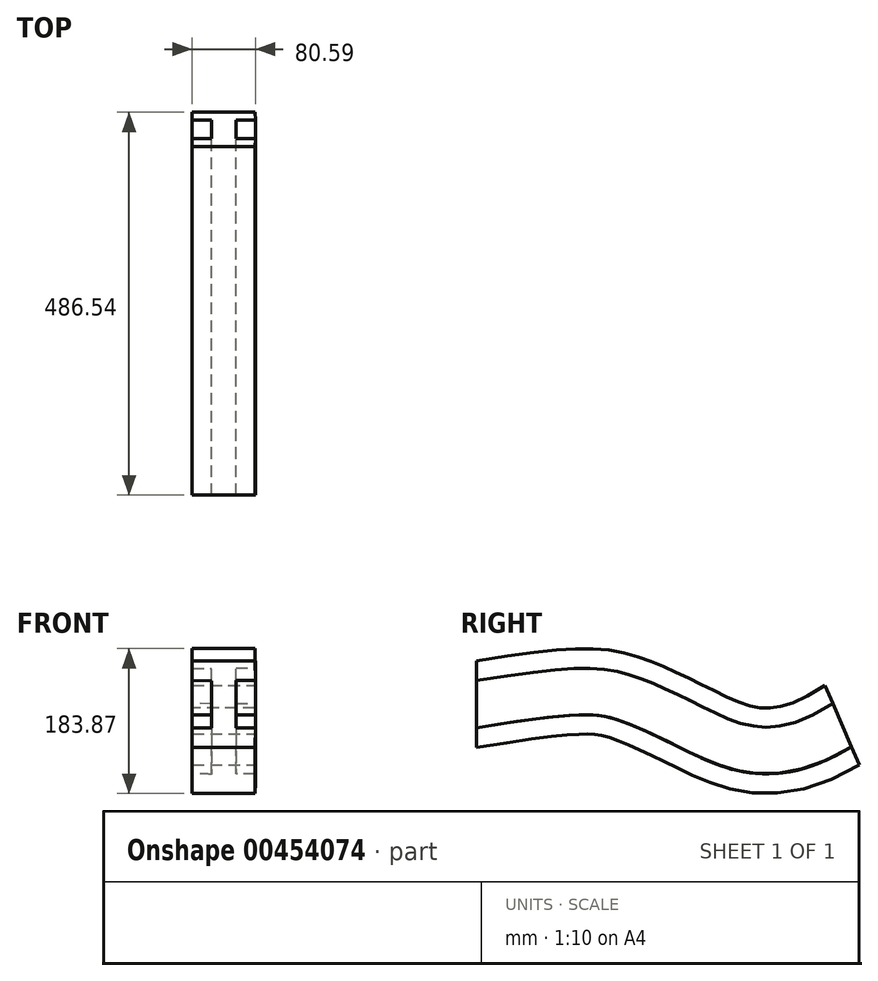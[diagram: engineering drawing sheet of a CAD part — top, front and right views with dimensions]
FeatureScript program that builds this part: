
annotation { "Feature Type Name" : "Feature", "Feature Type Description" : "" }
export const myFeature = defineFeature(function(context is Context, id is Id, definition is map)
    precondition{}
    {
        {
            var Q0;
            Q0=qCreatedBy(makeId("Front.planeOp"),FACE);
            var sketch = newSketch(context, id + "F0", { "sketchPlane" : qUnion([Q0])});
            skLineSegment(sketch, "E0", {"start": v(-41.1, 54.65) * mm, "end": v(38.9, 54.65) * mm});
            skLineSegment(sketch, "E1", {"start": v(-40.8, -55.35) * mm, "end": v(39.2, -55.35) * mm});
            skLineSegment(sketch, "E2", {"start": v(-16.1, 29.23) * mm, "end": v(-16.1, -30.77) * mm});
            skLineSegment(sketch, "E3", {"start": v(14.5, 29.66) * mm, "end": v(14.5, -30.34) * mm});
            skLineSegment(sketch, "E4", {"start": v(-41.1, 54.65) * mm, "end": v(-41.1, 29.65) * mm});
            skLineSegment(sketch, "E5", {"start": v(-16.1, 29.23) * mm, "end": v(-41.1, 29.65) * mm});
            skLineSegment(sketch, "E6", {"start": v(14.5, 29.66) * mm, "end": v(39.5, 29.66) * mm});
            skLineSegment(sketch, "E7", {"start": v(39.5, 29.66) * mm, "end": v(38.9, 54.65) * mm});
            skLineSegment(sketch, "E8", {"start": v(-16.1, -30.77) * mm, "end": v(-41.1, -30.35) * mm});
            skLineSegment(sketch, "E9", {"start": v(-41.1, -30.35) * mm, "end": v(-40.8, -55.35) * mm});
            skLineSegment(sketch, "E10", {"start": v(14.5, -30.34) * mm, "end": v(39.5, -30.35) * mm});
            skLineSegment(sketch, "E11", {"start": v(39.5, -30.35) * mm, "end": v(39.2, -55.35) * mm});
            skSolve(sketch);
        }
        {
            var Q0;
            Q0=qCreatedBy(makeId("Right.planeOp"),FACE);
            var sketch = newSketch(context, id + "F1", { "sketchPlane" : qUnion([Q0])});
            skFitSpline(sketch, "E12", {"points": [v(0, 0) * mm, v(188, 8.39) * mm, v(280.93, -33.1) * mm, v(464.58, -26.6) * mm], "startDerivative": vector(982.31, 155) * mm, "endDerivative": vector(700.8, 443.68) * mm});
            skSolve(sketch);
        }
        {
            var Q0;
            Q0=makeQuery(id+"F0.imprint","IMPRINT",FACE,{"disambiguationData":[TD([[makeQuery(id+"F0.imprint","IMPRINT",EDGE,{"derivedFrom":sQuery(id+"F0.wireOp",EDGE,"E0")}),-1.0]])]});
            var Q1;
            Q1=sQuery(id+"F1.wireOp",EDGE,"E12");
            sweep(context, id + "F2", {"profiles" : qUnion([Q0]), "path" : qUnion([Q1])});
        }
    });
